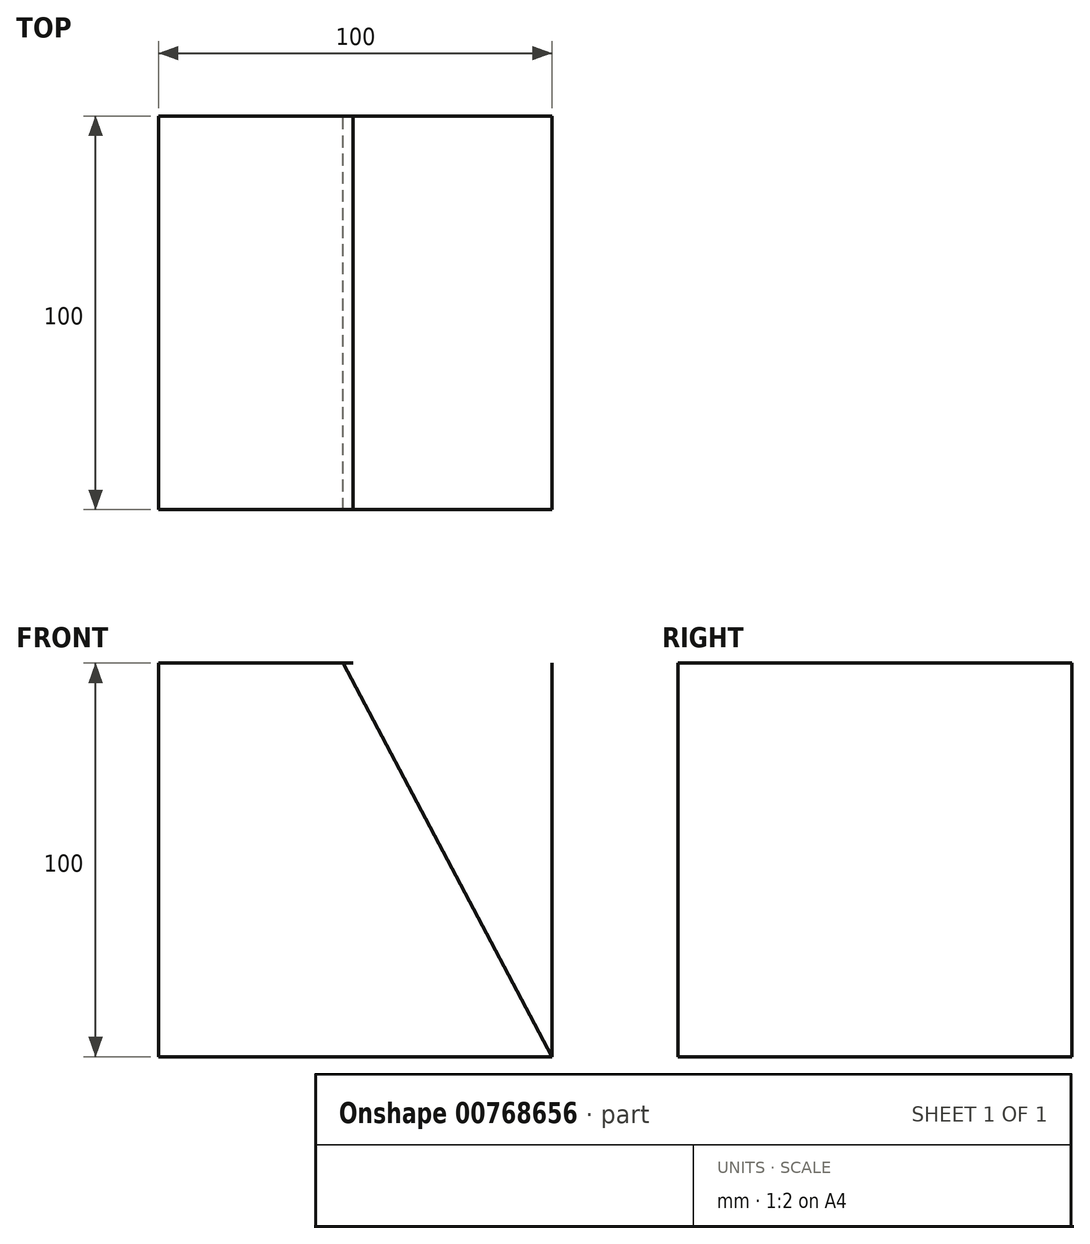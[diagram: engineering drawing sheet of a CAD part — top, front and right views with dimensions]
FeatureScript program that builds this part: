
annotation { "Feature Type Name" : "Feature", "Feature Type Description" : "" }
export const myFeature = defineFeature(function(context is Context, id is Id, definition is map)
    precondition{}
    {
        {
            var Q0;
            Q0=qCreatedBy(makeId("Top.planeOp"),FACE);
            var sketch = newSketch(context, id + "F0", { "sketchPlane" : qUnion([Q0])});
            skLineSegment(sketch, "E0.bottom", {"start": v(-45.45, 40) * mm, "end": v(54.55, 40) * mm});
            skLineSegment(sketch, "E0.top", {"start": v(-45.45, -60) * mm, "end": v(54.55, -60) * mm});
            skLineSegment(sketch, "E0.left", {"start": v(-45.45, 40) * mm, "end": v(-45.45, -60) * mm});
            skLineSegment(sketch, "E0.right", {"start": v(54.55, 40) * mm, "end": v(54.55, -60) * mm});
            skSolve(sketch);
        }
        {
            var Q0;
            Q0 = qSketchRegion(id + "F0", true);
            extrude(context, id + "F1", {"entities" : qUnion([Q0]), "depth" : 100 * mm, "offsetDistance" : 25 * mm});
        }
        {
            var Q0;
            Q0=qCreatedBy(makeId("Front.planeOp"),FACE);
            var sketch = newSketch(context, id + "F2", { "sketchPlane" : qUnion([Q0])});
            skLineSegment(sketch, "E1", {"start": v(54.5, 100.56) * mm, "end": v(54.5, 0) * mm});
            skLineSegment(sketch, "E2", {"start": v(54.5, 0) * mm, "end": v(1.47, 99.97) * mm});
            skLineSegment(sketch, "E3", {"start": v(1.47, 99.97) * mm, "end": v(54.5, 100.56) * mm});
            skSolve(sketch);
        }
        {
            var Q0;
            Q0 = qSketchRegion(id + "F2", true);
            extrude(context, id + "F3", {"entities" : qUnion([Q0]), "operationType" : NewBodyOperationType.REMOVE, "endBound" : BoundingType.SYMMETRIC, "depth" : 170 * mm, "offsetDistance" : 25 * mm});
        }
    });
